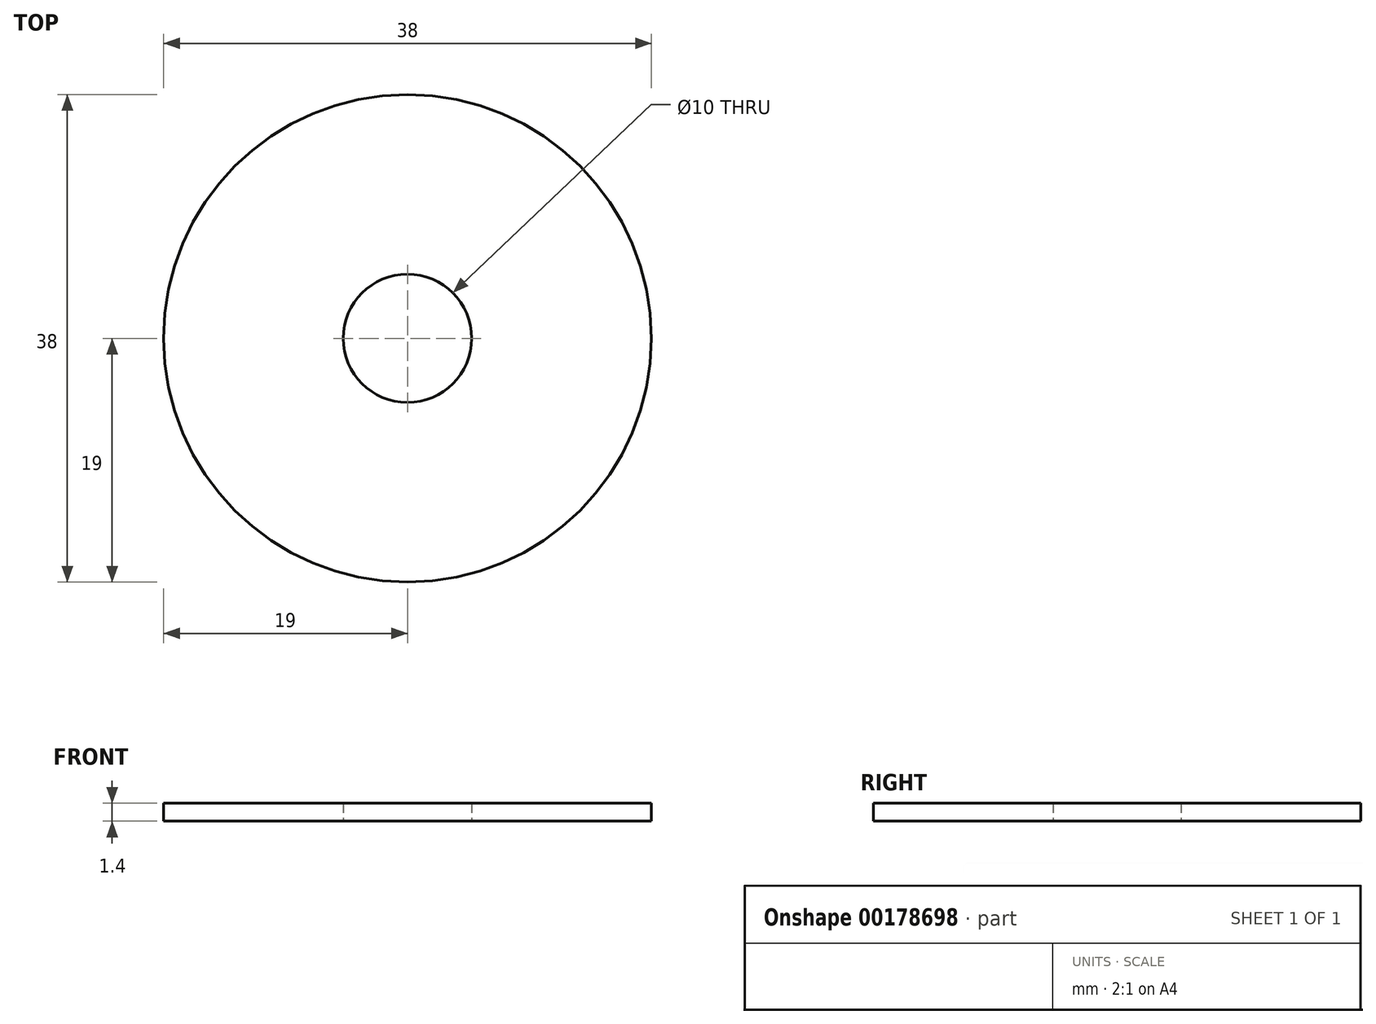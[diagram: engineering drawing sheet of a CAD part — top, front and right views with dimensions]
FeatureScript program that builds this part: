
annotation { "Feature Type Name" : "Feature", "Feature Type Description" : "" }
export const myFeature = defineFeature(function(context is Context, id is Id, definition is map)
    precondition{}
    {
        {
            var Q0;
            Q0=qCreatedBy(makeId("Top.planeOp"),FACE);
            var sketch = newSketch(context, id + "F0", { "sketchPlane" : qUnion([Q0])});
            skCircle(sketch, "E0", {"center": v(0, 0) * mm, "radius": 19 * mm});
            skCircle(sketch, "E1", {"center": v(0, 0) * mm, "radius": 5 * mm});
            skSolve(sketch);
        }
        {
            var Q0;
            Q0 = qSketchRegion(id + "F0", true);
            extrude(context, id + "F1", {"entities" : qUnion([Q0]), "depth" : 1.4 * mm});
        }
    });
